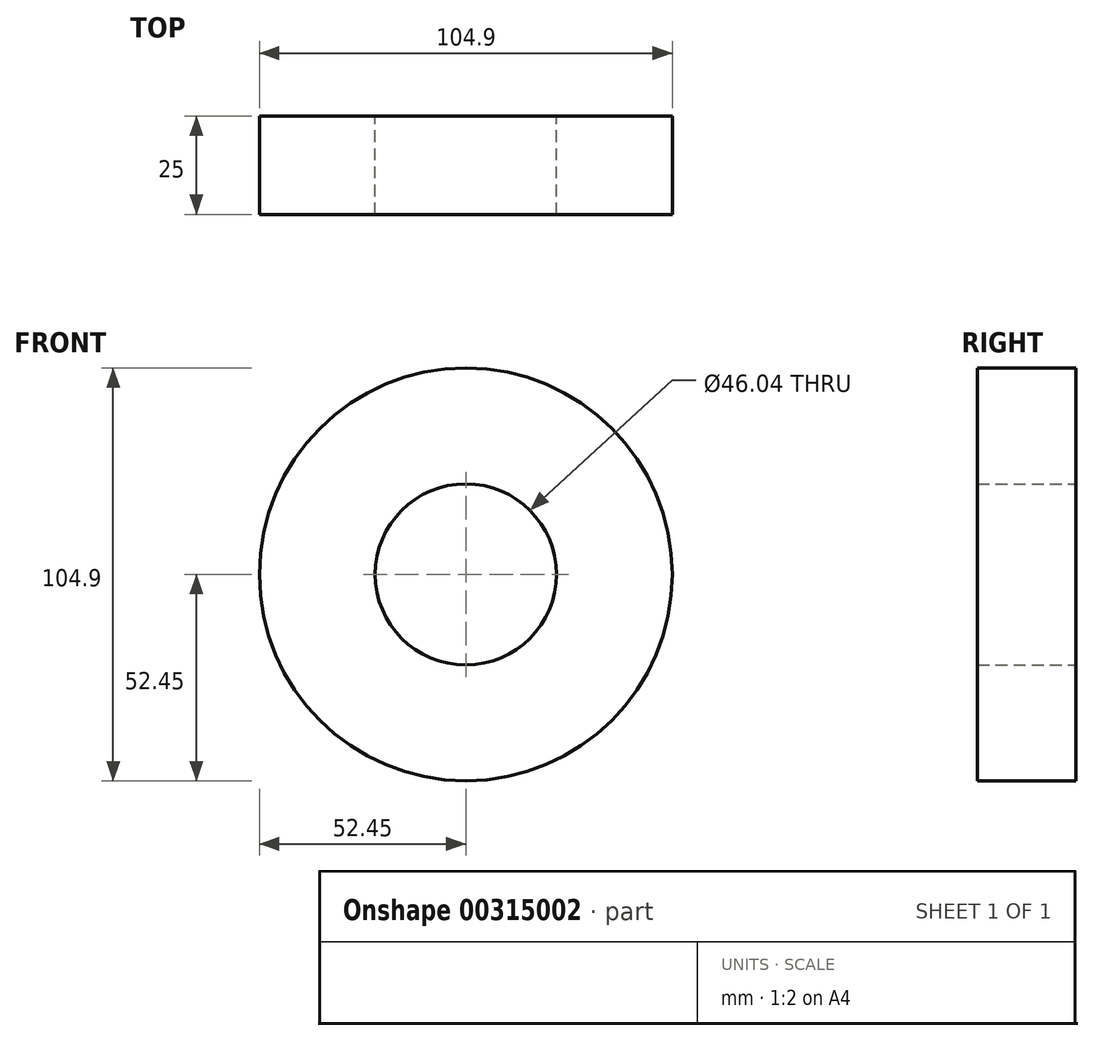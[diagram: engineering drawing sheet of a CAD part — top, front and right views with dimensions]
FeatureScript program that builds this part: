
annotation { "Feature Type Name" : "Feature", "Feature Type Description" : "" }
export const myFeature = defineFeature(function(context is Context, id is Id, definition is map)
    precondition{}
    {
        {
            var Q0;
            Q0=qCreatedBy(makeId("Front.planeOp"),FACE);
            var sketch = newSketch(context, id + "F0", { "sketchPlane" : qUnion([Q0])});
            skCircle(sketch, "E0", {"center": v(0, 0) * mm, "radius": 52.45 * mm});
            skCircle(sketch, "E1", {"center": v(0, 0) * mm, "radius": 23.02 * mm});
            skSolve(sketch);
        }
        {
            var Q0;
            Q0 = qSketchRegion(id + "F0", true);
            extrude(context, id + "F1", {"entities" : qUnion([Q0]), "depth" : 25 * mm});
        }
    });
